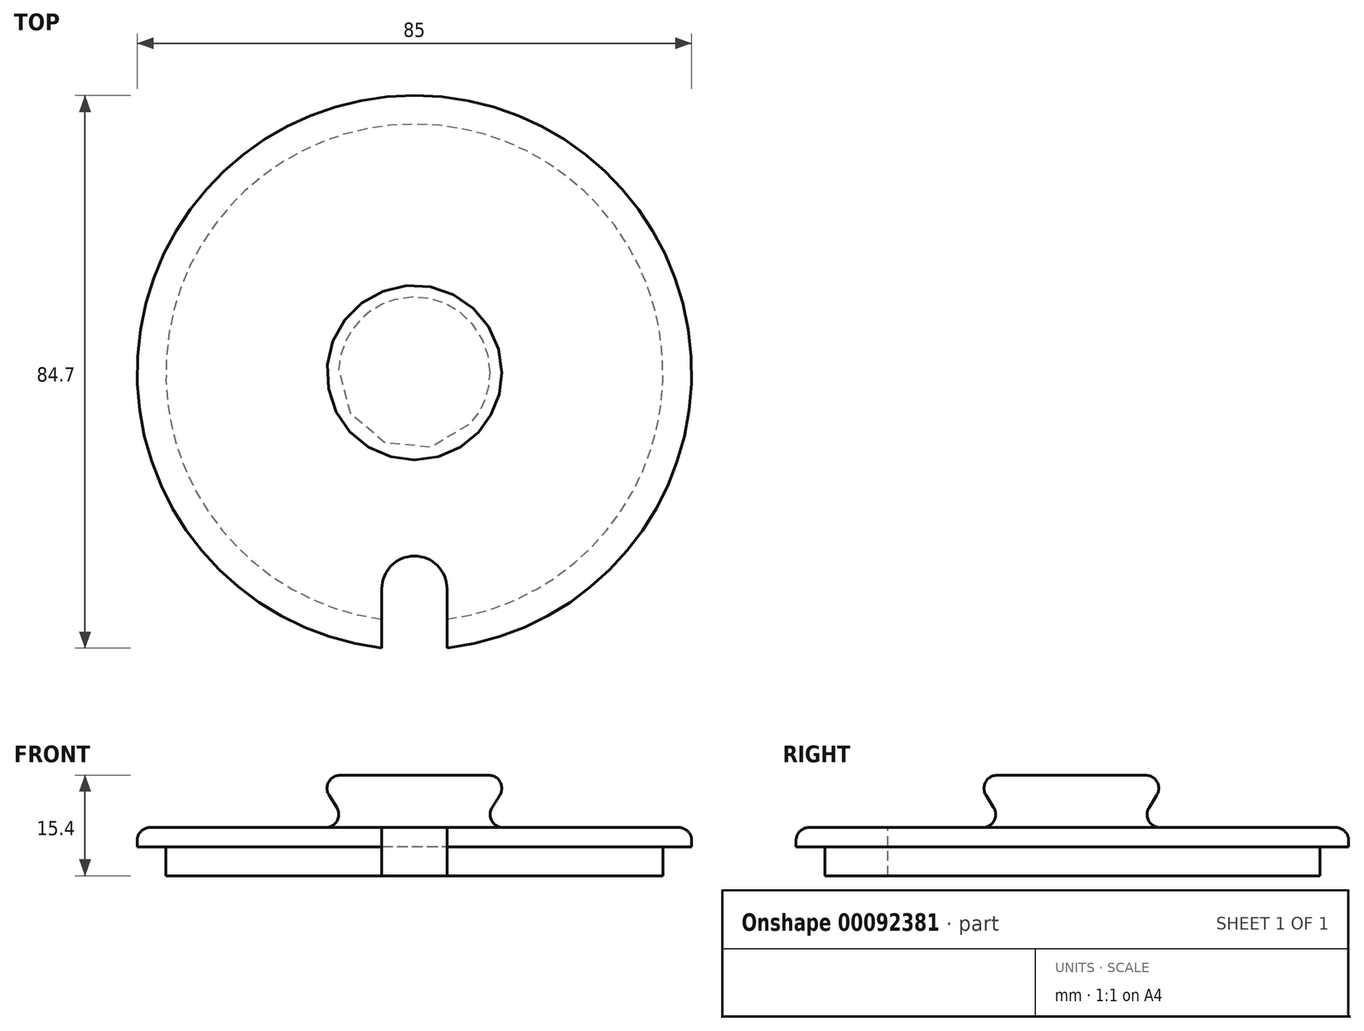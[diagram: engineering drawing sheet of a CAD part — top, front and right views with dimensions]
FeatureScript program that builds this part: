
annotation { "Feature Type Name" : "Feature", "Feature Type Description" : "" }
export const myFeature = defineFeature(function(context is Context, id is Id, definition is map)
    precondition{}
    {
        {
            var Q0;
            Q0=qCreatedBy(makeId("Front.planeOp"),FACE);
            var sketch = newSketch(context, id + "F0", { "sketchPlane" : qUnion([Q0])});
            skLineSegment(sketch, "E0", {"start": v(38.1, 0) * mm, "end": v(38.1, 4.4) * mm});
            skLineSegment(sketch, "E1", {"start": v(38.1, 4.4) * mm, "end": v(42.5, 4.4) * mm});
            skLineSegment(sketch, "E2", {"start": v(42.5, 4.4) * mm, "end": v(42.5, 5.4) * mm});
            skLineSegment(sketch, "E3", {"start": v(0, 0) * mm, "end": v(38.1, 0) * mm});
            skLineSegment(sketch, "E4", {"start": v(0, 69.98) * mm, "end": v(0, -47.1) * mm, "construction": true});
            skLineSegment(sketch, "E5", {"start": v(0, 15.4) * mm, "end": v(0, 0) * mm});
            skLineSegment(sketch, "E6", {"start": v(40.5, 7.4) * mm, "end": v(13.6, 7.4) * mm});
            skLineSegment(sketch, "E7", {"start": v(11.91, 10.46) * mm, "end": v(13.09, 12.34) * mm});
            skLineSegment(sketch, "E8", {"start": v(11.4, 15.4) * mm, "end": v(0, 15.4) * mm});
            skPoint(sketch, "E9.visualSharp", {"position": v(15, 15.4) * mm});
            skArc(sketch, "E9.filletArc", {"start": v(13.09, 12.34) * mm, "mid": v(13.14, 14.37) * mm, "end": v(11.4, 15.4) * mm});
            skPoint(sketch, "E10.visualSharp", {"position": v(10, 7.4) * mm});
            skArc(sketch, "E10.filletArc", {"start": v(11.91, 10.46) * mm, "mid": v(11.86, 8.43) * mm, "end": v(13.6, 7.4) * mm});
            skPoint(sketch, "E11.visualSharp", {"position": v(42.5, 7.4) * mm});
            skArc(sketch, "E11.filletArc", {"start": v(42.5, 5.4) * mm, "mid": v(41.91, 6.81) * mm, "end": v(40.5, 7.4) * mm});
            skSolve(sketch);
        }
        {
            var Q0;
            Q0=makeQuery(id+"F0.imprint","IMPRINT",FACE,{"disambiguationData":[TD([[makeQuery(id+"F0.imprint","IMPRINT",EDGE,{"derivedFrom":sQuery(id+"F0.wireOp",EDGE,"E0")}),1.0]])]});
            var Q1;
            Q1=sQuery(id+"F0.wireOp",EDGE,"E4");
            revolve(context, id + "F1", {"entities" : qUnion([Q0]), "axis" : qUnion([Q1]), "revolveType" : RevolveType.FULL});
        }
        {
            var Q0;
            Q0=qCreatedBy(makeId("Top.planeOp"),FACE);
            var sketch = newSketch(context, id + "F2", { "sketchPlane" : qUnion([Q0])});
            skLineSegment(sketch, "E12.bottom", {"start": v(-5, 0) * mm, "end": v(5, 0) * mm});
            skLineSegment(sketch, "E12.top", {"start": v(-5, -42.5) * mm, "end": v(5, -42.5) * mm});
            skLineSegment(sketch, "E12.left", {"start": v(-5, 0) * mm, "end": v(-5, -42.5) * mm});
            skLineSegment(sketch, "E12.right", {"start": v(5, 0) * mm, "end": v(5, -42.5) * mm});
            skPoint(sketch, "E13", {"position": v(-5, -33.1) * mm});
            skPoint(sketch, "E14", {"position": v(5, -33.1) * mm});
            skPoint(sketch, "E15", {"position": v(0, 0) * mm});
            skLineSegment(sketch, "E16", {"start": v(0, 9.58) * mm, "end": v(0, -48.06) * mm, "construction": true});
            skArc(sketch, "E17", {"start": v(-5, -33.1) * mm, "mid": v(0, -28.1) * mm, "end": v(5, -33.1) * mm});
            skSolve(sketch);
        }
        {
            var Q0;
            {var subQ0=sQuery(id+"F2.wireOp",EDGE,"E12.top");Q0=makeQuery(id+"F2.imprint","IMPRINT",FACE,{"disambiguationData":[TD([[makeQuery(id+"F2.imprint","IMPRINT",EDGE,{"derivedFrom":subQ0}),1.0]])]});}
            extrude(context, id + "F3", {"entities" : qUnion([Q0]), "operationType" : NewBodyOperationType.REMOVE, "endBound" : BoundingType.THROUGH_ALL, "oppositeDirection" : true, "depth" : 25 * mm, "hasSecondDirection" : true, "secondDirectionBound" : SecondDirectionBoundingType.THROUGH_ALL, "secondDirectionOppositeDirection" : false, "secondDirectionDepth" : 25 * mm});
        }
    });
